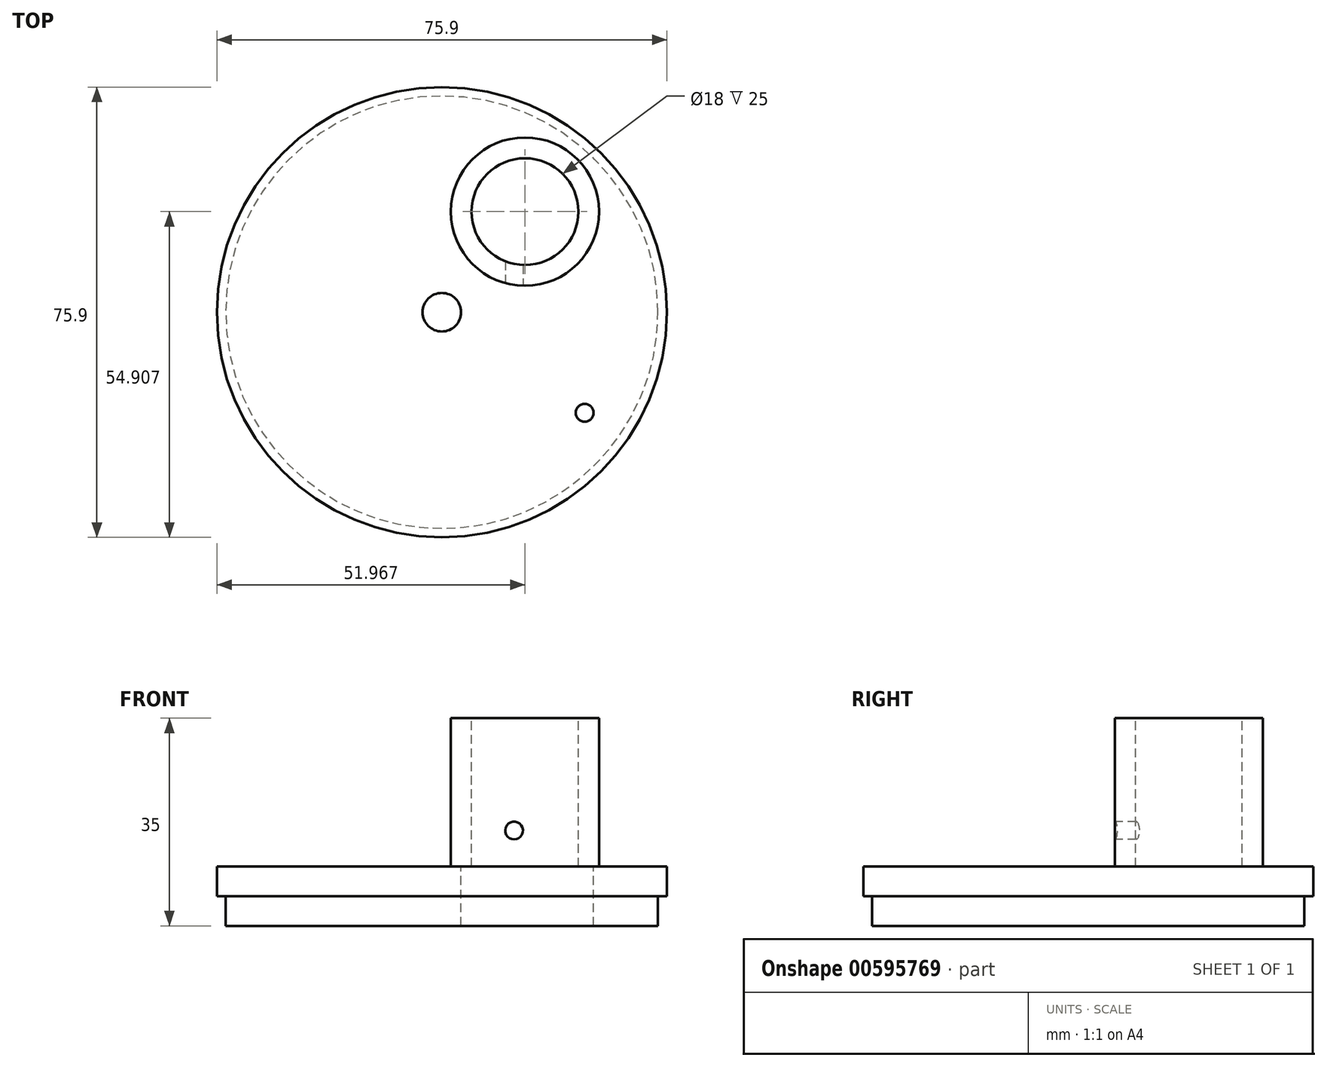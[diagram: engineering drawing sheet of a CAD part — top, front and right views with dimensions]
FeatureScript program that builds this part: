
annotation { "Feature Type Name" : "Feature", "Feature Type Description" : "" }
export const myFeature = defineFeature(function(context is Context, id is Id, definition is map)
    precondition{}
    {
        {
            var Q0;
            Q0=qCreatedBy(makeId("Top.planeOp"),FACE);
            var sketch = newSketch(context, id + "F0", { "sketchPlane" : qUnion([Q0])});
            skCircle(sketch, "E0", {"center": v(0, 0) * mm, "radius": 37.95 * mm});
            skSolve(sketch);
        }
        {
            var Q0;
            Q0 = qSketchRegion(id + "F0", true);
            extrude(context, id + "F1", {"entities" : qUnion([Q0]), "depth" : 5 * mm, "offsetDistance" : 25 * mm});
        }
        {
            var Q0;
            Q0=makeQuery(id+"F1.opExtrude","CAP_FACE",FACE,{"disambiguationData":[OSD([sQuery(id+"F0.wireOp",EDGE,"E0")])],"isStart":true});
            var sketch = newSketch(context, id + "F2", { "sketchPlane" : qUnion([Q0])});
            skCircle(sketch, "E1", {"center": v(0, 0) * mm, "radius": 36.45 * mm});
            skSolve(sketch);
        }
        {
            var Q0;
            Q0 = qSketchRegion(id + "F2", true);
            extrude(context, id + "F3", {"entities" : qUnion([Q0]), "operationType" : NewBodyOperationType.ADD, "depth" : 5 * mm, "offsetDistance" : 25 * mm});
        }
        {
            var Q0;
            Q0=makeQuery(id+"F1.opExtrude","CAP_FACE",FACE,{"disambiguationData":[OSD([sQuery(id+"F0.wireOp",EDGE,"E0")])],"isStart":false});
            var sketch = newSketch(context, id + "F4", { "sketchPlane" : qUnion([Q0])});
            skCircle(sketch, "E2", {"center": v(0, 0) * mm, "radius": 3.25 * mm});
            skSolve(sketch);
        }
        {
            var Q0;
            Q0 = qSketchRegion(id + "F4", true);
            extrude(context, id + "F5", {"entities" : qUnion([Q0]), "operationType" : NewBodyOperationType.REMOVE, "oppositeDirection" : true, "depth" : 10 * mm, "offsetDistance" : 25 * mm});
        }
        {
            var Q0;
            Q0=makeQuery(id+"F1.opExtrude","CAP_FACE",FACE,{"disambiguationData":[OSD([sQuery(id+"F0.wireOp",EDGE,"E0")])],"isStart":false});
            var sketch = newSketch(context, id + "F6", { "sketchPlane" : qUnion([Q0])});
            skCircle(sketch, "E3", {"center": v(14.02, 16.96) * mm, "radius": 12.5 * mm});
            skSolve(sketch);
        }
        {
            var Q0;
            Q0 = qSketchRegion(id + "F6", true);
            extrude(context, id + "F7", {"entities" : qUnion([Q0]), "operationType" : NewBodyOperationType.ADD, "depth" : 25 * mm, "offsetDistance" : 25 * mm});
        }
        {
            var Q0;
            Q0=makeQuery(id+"F7.opExtrude","CAP_FACE",FACE,{"disambiguationData":[OSD([sQuery(id+"F6.wireOp",EDGE,"E3")])],"isStart":false});
            var sketch = newSketch(context, id + "F8", { "sketchPlane" : qUnion([Q0])});
            skCircle(sketch, "E4", {"center": v(14.02, 16.96) * mm, "radius": 9 * mm});
            skSolve(sketch);
        }
        {
            var Q0;
            Q0 = qSketchRegion(id + "F8", true);
            extrude(context, id + "F9", {"entities" : qUnion([Q0]), "operationType" : NewBodyOperationType.REMOVE, "oppositeDirection" : true, "depth" : 25 * mm, "offsetDistance" : 25 * mm});
        }
        {
            var Q0;
            Q0=makeQuery(id+"F1.opExtrude","CAP_FACE",FACE,{"disambiguationData":[OSD([sQuery(id+"F0.wireOp",EDGE,"E0")])],"isStart":false});
            var sketch = newSketch(context, id + "F10", { "sketchPlane" : qUnion([Q0])});
            skCircle(sketch, "E5", {"center": v(24.09, -16.96) * mm, "radius": 1.5 * mm});
            skSolve(sketch);
        }
        {
            var Q0;
            Q0 = qSketchRegion(id + "F10", true);
            extrude(context, id + "F11", {"entities" : qUnion([Q0]), "operationType" : NewBodyOperationType.REMOVE, "oppositeDirection" : true, "depth" : 10 * mm, "offsetDistance" : 25 * mm});
        }
        {
            var Q0;
            Q0=qCreatedBy(makeId("Front.planeOp"),FACE);
            var sketch = newSketch(context, id + "F12", { "sketchPlane" : qUnion([Q0])});
            skCircle(sketch, "E6", {"center": v(12.18, 11.07) * mm, "radius": 1.5 * mm});
            skSolve(sketch);
        }
        {
            var Q0;
            Q0 = qSketchRegion(id + "F12", true);
            extrude(context, id + "F13", {"entities" : qUnion([Q0]), "operationType" : NewBodyOperationType.REMOVE, "oppositeDirection" : true, "depth" : 10 * mm, "offsetDistance" : 25 * mm});
        }
    });
